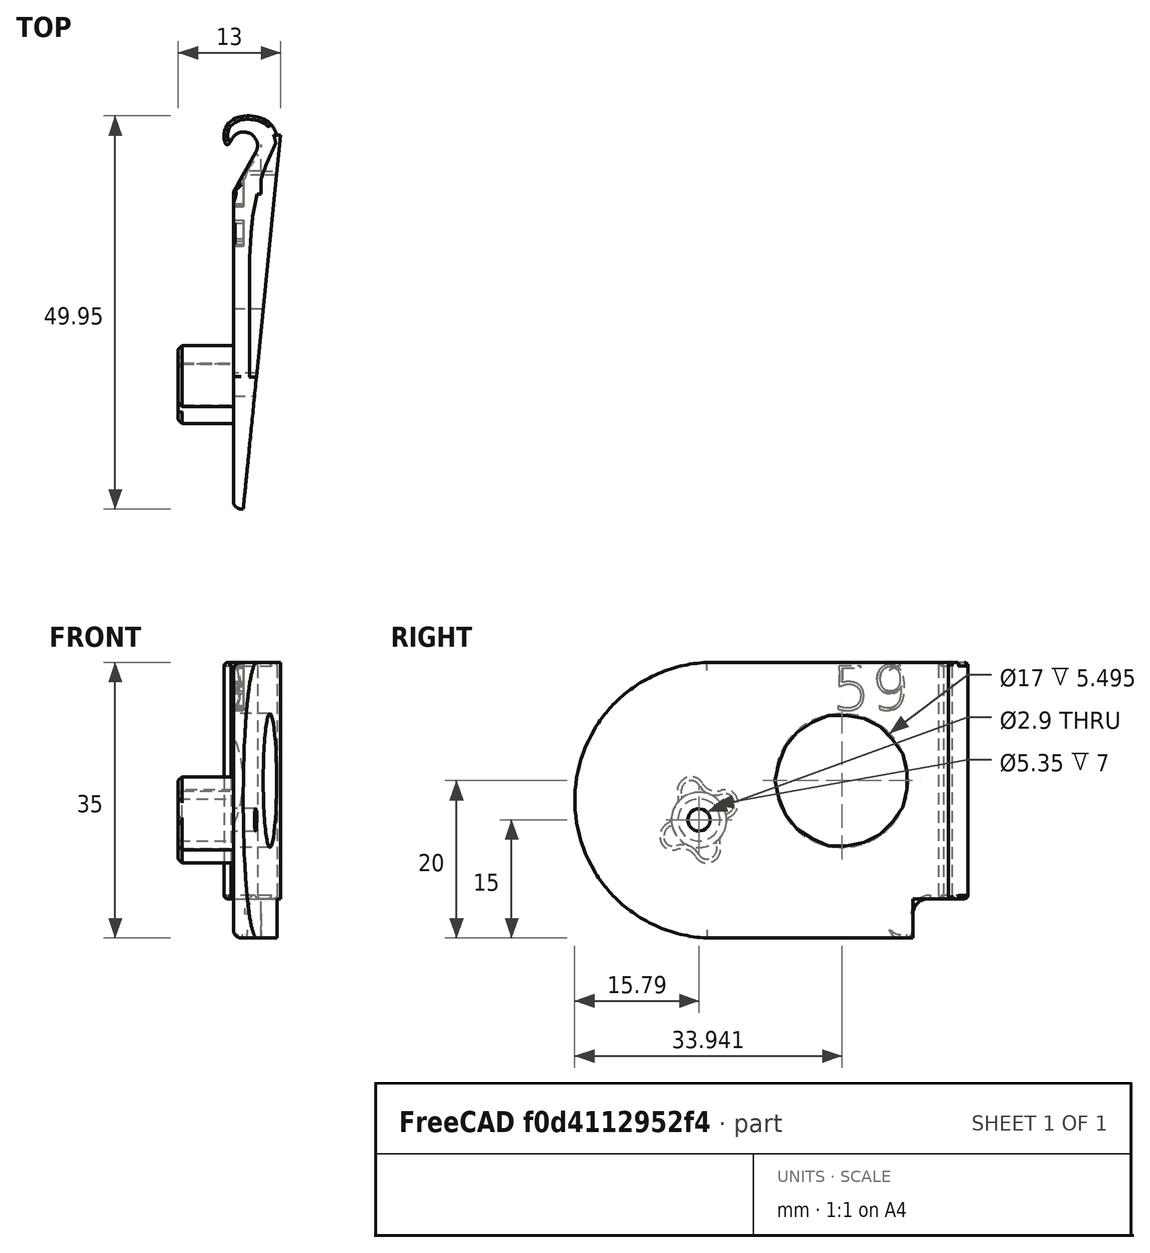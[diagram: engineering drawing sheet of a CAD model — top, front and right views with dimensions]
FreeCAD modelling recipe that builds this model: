
FCSTD DOCUMENT  (FreeCAD 0.18R)
Label: hinge-right-159deg-angled
License: All rights reserved
LicenseURL: http://en.wikipedia.org/wiki/All_rights_reserved
objects: App::FeaturePython×4, Part::FeaturePython×2, Part::Part2DObjectPython×1, Part::Extrusion×1, Part::Cut×1
note: 5 computed .brp shape members not serialized (recipe doc carries the construction recipe); baked Part::Feature solids carry a one-line shape summary decoded from their .brp

FEATURE [Part::FeaturePython] pillar_base_001  label="pillar-base_001"  # a2plus imported part (geometry in sourceFile) (typed FeaturePython)
  Placement = pos=(0.000608724,-57.1574,24.256) rot=(-1,0,0;0.802677rad)
  a2p_Version = V0.1
  fixedPosition = false
  objectType = a2pPart
  sourceFile = ./parts/pillar-base.fcstd
  subassemblyImport = false
  timeLastImport = 1.60452e+09
  updateColors = true
FEATURE [Part::Part2DObjectPython] ShapeString  # Draft 2D object (typed FeaturePython)
  FontFile = <path>
  Placement = pos=(1.61,10.5,29) rot=(0.57735,-0.57735,-0.57735;2.0944rad)
  Size = 6
  String = 59
  Tracking = 0
FEATURE [Part::Extrusion] Extrude
  Base = -> ShapeString
  Dir = (-1,0,0)
  DirMode = 2
  FaceMakerClass = Part::FaceMakerBullseye
  LengthFwd = 3.5
  LengthRev = 0
  Placement = pos=(0,0,0) rot=(0,0,1;3.14159rad)
  Solid = false
  Symmetric = false
FEATURE [Part::FeaturePython] bracket_right_angled_001  label="bracket-right-angled_001"  # a2plus imported part (geometry in sourceFile) (typed FeaturePython)
  Placement = pos=(0,0,0) rot=(0,0,1;3.14159rad)
  a2p_Version = V0.1
  fixedPosition = true
  objectType = a2pPart
  sourceFile = ./parts/bracket-right-angled.fcstd
  subassemblyImport = false
  timeLastImport = 1.60454e+09
  updateColors = true
FEATURE [App::FeaturePython] axisCoincident_001  label="axisCoincident_001__bracket-right-angled_001"  # a2plus constraint (typed FeaturePython)
  Object1 = pillar_base_001
  Object2 = bracket_right_angled_001
  ParentTreeObject = -> pillar_base_001
  SubElement1 = Face17
  SubElement2 = Face27
  Suppressed = false
  Type = axial
  directionConstraint = 1
  lockRotation = false
FEATURE [App::FeaturePython] axisCoincident_001_mirror  label="axisCoincident_001__pillar-base_001"  # a2plus constraint (typed FeaturePython)
  Object1 = pillar_base_001
  Object2 = bracket_right_angled_001
  ParentTreeObject = -> bracket_right_angled_001
  SubElement1 = Face17
  SubElement2 = Face27
  Suppressed = false
  Type = axial
  directionConstraint = 1
  lockRotation = false
FEATURE [App::FeaturePython] planeCoincident_001  label="planeCoincident_001__bracket-right-angled_001"  # a2plus constraint (typed FeaturePython)
  Object1 = pillar_base_001
  Object2 = bracket_right_angled_001
  ParentTreeObject = -> pillar_base_001
  SubElement1 = Face1
  SubElement2 = Face55
  Suppressed = false
  Type = plane
  directionConstraint = 1
  offset = 0
FEATURE [App::FeaturePython] planeCoincident_001_mirror  label="planeCoincident_001__pillar-base_001"  # a2plus constraint (typed FeaturePython)
  Object1 = pillar_base_001
  Object2 = bracket_right_angled_001
  ParentTreeObject = -> bracket_right_angled_001
  SubElement1 = Face1
  SubElement2 = Face55
  Suppressed = false
  Type = plane
  directionConstraint = 1
  offset = 0
FEATURE [Part::Cut] Cut
  Base = -> bracket_right_angled_001
  Tool = -> Extrude
note: 1 file-system path scrubbed to <path> (originals preserved in the JSON sidecar)
